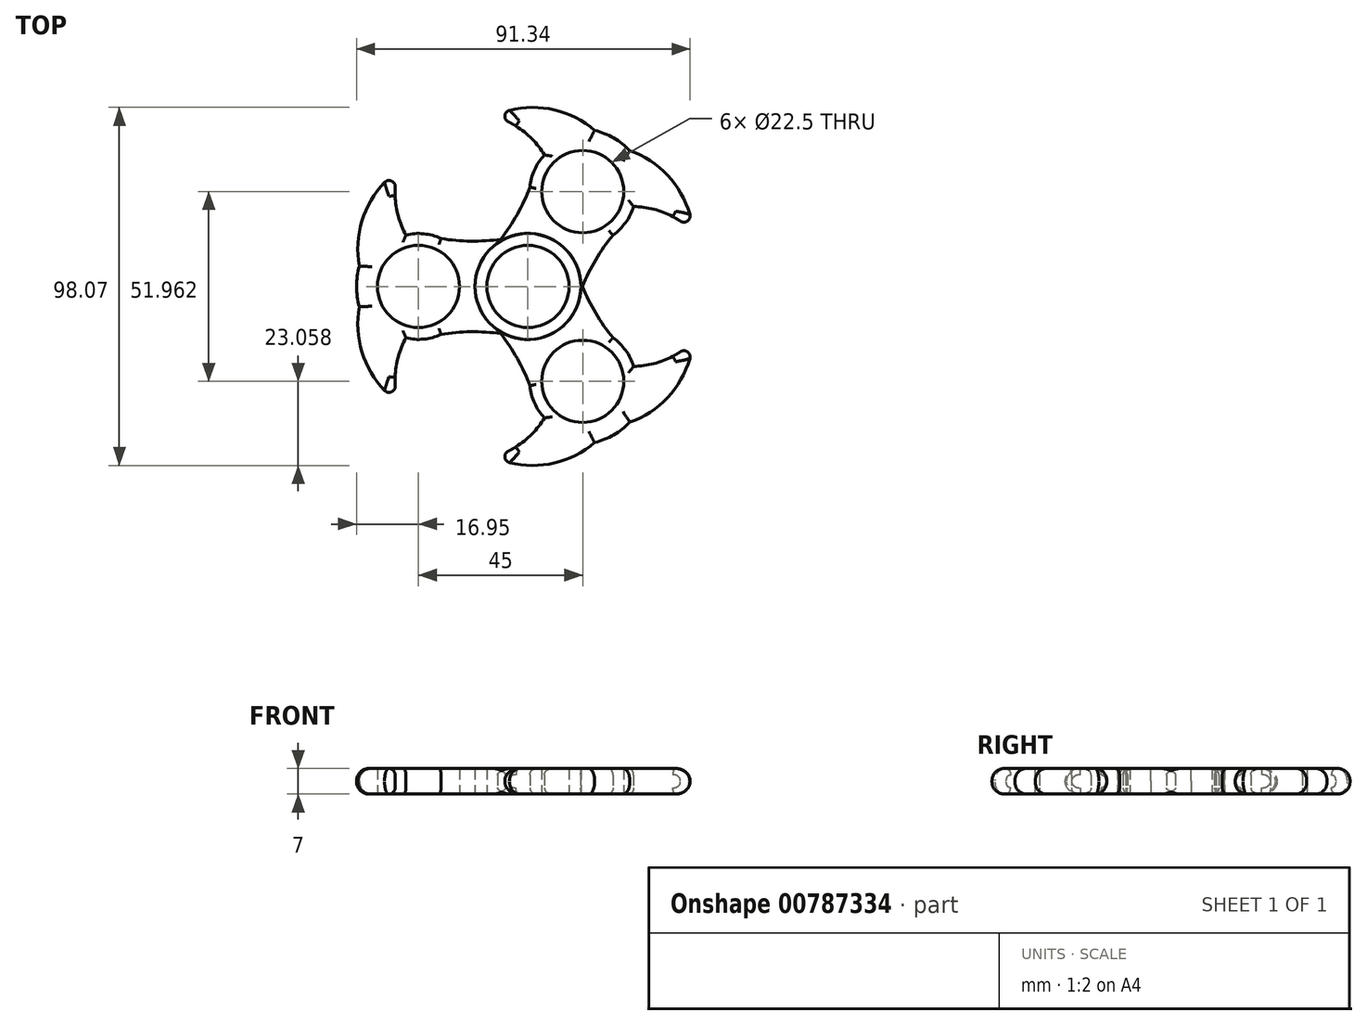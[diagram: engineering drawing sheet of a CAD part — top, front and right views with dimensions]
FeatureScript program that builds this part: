
annotation { "Feature Type Name" : "Feature", "Feature Type Description" : "" }
export const myFeature = defineFeature(function(context is Context, id is Id, definition is map)
    precondition{}
    {
        {
            var Q0;
            Q0=qCreatedBy(makeId("Top.planeOp"),FACE);
            var sketch = newSketch(context, id + "F0", { "sketchPlane" : qUnion([Q0])});
            skCircle(sketch, "E0", {"center": v(0, 0) * mm, "radius": 11.25 * mm});
            skLineSegment(sketch, "E1", {"start": v(0, 0) * mm, "end": v(-30, 0) * mm});
            skCircle(sketch, "E2", {"center": v(-30, 0) * mm, "radius": 11.25 * mm});
            skCircle(sketch, "E3", {"center": v(-30, 0) * mm, "radius": 14.5 * mm});
            skCircle(sketch, "E4", {"center": v(0, 0) * mm, "radius": 14.5 * mm});
            skArc(sketch, "E5", {"start": v(0, -14.5) * mm, "mid": v(-15, -12.4) * mm, "end": v(-30, -14.5) * mm});
            skArc(sketch, "E6.MirrorCS", {"start": v(0, 14.5) * mm, "mid": v(-15, 12.41) * mm, "end": v(-30, 14.5) * mm});
            skArc(sketch, "E7", {"start": v(-33.43, -14.08) * mm, "mid": v(-36.22, -22.63) * mm, "end": v(-35.67, -31.61) * mm});
            skArc(sketch, "E8", {"start": v(-44.5, 0) * mm, "mid": v(-45.64, -17.36) * mm, "end": v(-35.67, -31.61) * mm});
            skArc(sketch, "E9.MirrorCS", {"start": v(-33.43, 14.1) * mm, "mid": v(-36.22, 22.65) * mm, "end": v(-35.67, 31.63) * mm});
            skArc(sketch, "E10.MirrorCS", {"start": v(-44.5, 0.02) * mm, "mid": v(-45.64, 17.38) * mm, "end": v(-35.67, 31.63) * mm});
            skLineSegment(sketch, "E11", {"start": v(-44.5, 0.02) * mm, "end": v(-46.18, 0.02) * mm});
            skArc(sketch, "E12", {"start": v(-46.18, 5.59) * mm, "mid": v(-46.95, 0) * mm, "end": v(-46.18, -5.57) * mm});
            skSolve(sketch);
        }
        {
            var Q0;
            Q0=qSketchRegion(id+"F0",true);
            extrude(context, id + "F1", {"entities" : qUnion([Q0]), "depth" : 7 * mm, "offsetDistance" : 25 * mm});
        }
        {
            var Q0;
            Q0=makeQuery(id+"F1.opExtrude","SWEPT_BODY",BODY,{"disambiguationData":[OSD([sQuery(id+"F0.wireOp",EDGE,"E0"),sQuery(id+"F0.wireOp",EDGE,"E2"),sQuery(id+"F0.wireOp",EDGE,"E3"),sQuery(id+"F0.wireOp",EDGE,"E4"),sQuery(id+"F0.wireOp",EDGE,"E5"),sQuery(id+"F0.wireOp",EDGE,"E6.MirrorCS"),sQuery(id+"F0.wireOp",EDGE,"N5z0aknD-i1vi-YF0C-1aPX-2y42hYEXv3Ia"),sQuery(id+"F0.wireOp",EDGE,"vDmnVq8P-OYbs-Mt9C-JsBL-gKGyEo7dJEWc")])]});
            var Q1;
            Q1=makeQuery(id+"F1.opExtrude","SWEPT_FACE",FACE,{"disambiguationData":[OSD([sQuery(id+"F0.wireOp",EDGE,"E4")])]});
            circularPattern(context, id + "F2", {"entities" : qUnion([Q0]), "axis" : qUnion([Q1]), "angle" : 360 * degree, "instanceCount" : 3, "equalSpace" : true});
        }
        {
            var Q0;
            Q0=makeQuery(id+"F2.opPattern","COPY",EDGE,{"derivedFrom":makeQuery(id+"F1.opExtrude","CAP_EDGE",EDGE,{"disambiguationData":[OSD([sQuery(id+"F0.wireOp",EDGE,"E10.MirrorCS")])],"isStart":false}),"instanceName":"2"});
            var Q1;
            Q1=makeQuery(id+"F2.opPattern","COPY",EDGE,{"derivedFrom":makeQuery(id+"F1.opExtrude","CAP_EDGE",EDGE,{"disambiguationData":[OSD([sQuery(id+"F0.wireOp",EDGE,"E12")])],"isStart":false}),"instanceName":"2"});
            var Q2;
            Q2=makeQuery(id+"F2.opPattern","COPY",EDGE,{"derivedFrom":makeQuery(id+"F1.opExtrude","CAP_EDGE",EDGE,{"disambiguationData":[OSD([sQuery(id+"F0.wireOp",EDGE,"E8")])],"isStart":false}),"instanceName":"2"});
            var Q3;
            Q3=makeQuery(id+"F2.opPattern","COPY",EDGE,{"derivedFrom":makeQuery(id+"F1.opExtrude","CAP_EDGE",EDGE,{"disambiguationData":[OSD([sQuery(id+"F0.wireOp",EDGE,"E10.MirrorCS")])],"isStart":false}),"instanceName":"1"});
            var Q4;
            Q4=makeQuery(id+"F2.opPattern","COPY",EDGE,{"derivedFrom":makeQuery(id+"F1.opExtrude","CAP_EDGE",EDGE,{"disambiguationData":[OSD([sQuery(id+"F0.wireOp",EDGE,"E12")])],"isStart":false}),"instanceName":"1"});
            var Q5;
            Q5=makeQuery(id+"F2.opPattern","COPY",EDGE,{"derivedFrom":makeQuery(id+"F1.opExtrude","CAP_EDGE",EDGE,{"disambiguationData":[OSD([sQuery(id+"F0.wireOp",EDGE,"E8")])],"isStart":false}),"instanceName":"1"});
            var Q6;
            Q6=makeQuery(id+"F1.opExtrude","CAP_EDGE",EDGE,{"disambiguationData":[OSD([sQuery(id+"F0.wireOp",EDGE,"E10.MirrorCS")])],"isStart":false});
            var Q7;
            Q7=makeQuery(id+"F1.opExtrude","CAP_EDGE",EDGE,{"disambiguationData":[OSD([sQuery(id+"F0.wireOp",EDGE,"E12")])],"isStart":false});
            var Q8;
            Q8=makeQuery(id+"F1.opExtrude","CAP_EDGE",EDGE,{"disambiguationData":[OSD([sQuery(id+"F0.wireOp",EDGE,"E8")])],"isStart":false});
            var Q9;
            Q9=makeQuery(id+"F1.opExtrude","CAP_EDGE",EDGE,{"disambiguationData":[OSD([sQuery(id+"F0.wireOp",EDGE,"E12")])],"isStart":true});
            var Q10;
            Q10=makeQuery(id+"F1.opExtrude","CAP_EDGE",EDGE,{"disambiguationData":[OSD([sQuery(id+"F0.wireOp",EDGE,"E8")])],"isStart":true});
            var Q11;
            Q11=makeQuery(id+"F1.opExtrude","CAP_EDGE",EDGE,{"disambiguationData":[OSD([sQuery(id+"F0.wireOp",EDGE,"E10.MirrorCS")])],"isStart":true});
            var Q12;
            Q12=makeQuery(id+"F2.opPattern","COPY",EDGE,{"derivedFrom":makeQuery(id+"F1.opExtrude","CAP_EDGE",EDGE,{"disambiguationData":[OSD([sQuery(id+"F0.wireOp",EDGE,"E12")])],"isStart":true}),"instanceName":"2"});
            var Q13;
            Q13=makeQuery(id+"F2.opPattern","COPY",EDGE,{"derivedFrom":makeQuery(id+"F1.opExtrude","CAP_EDGE",EDGE,{"disambiguationData":[OSD([sQuery(id+"F0.wireOp",EDGE,"E8")])],"isStart":true}),"instanceName":"2"});
            var Q14;
            Q14=makeQuery(id+"F2.opPattern","COPY",EDGE,{"derivedFrom":makeQuery(id+"F1.opExtrude","CAP_EDGE",EDGE,{"disambiguationData":[OSD([sQuery(id+"F0.wireOp",EDGE,"E10.MirrorCS")])],"isStart":true}),"instanceName":"2"});
            var Q15;
            Q15=makeQuery(id+"F2.opPattern","COPY",EDGE,{"derivedFrom":makeQuery(id+"F1.opExtrude","CAP_EDGE",EDGE,{"disambiguationData":[OSD([sQuery(id+"F0.wireOp",EDGE,"E10.MirrorCS")])],"isStart":true}),"instanceName":"1"});
            var Q16;
            Q16=makeQuery(id+"F2.opPattern","COPY",EDGE,{"derivedFrom":makeQuery(id+"F1.opExtrude","CAP_EDGE",EDGE,{"disambiguationData":[OSD([sQuery(id+"F0.wireOp",EDGE,"E12")])],"isStart":true}),"instanceName":"1"});
            var Q17;
            Q17=makeQuery(id+"F2.opPattern","COPY",EDGE,{"derivedFrom":makeQuery(id+"F1.opExtrude","CAP_EDGE",EDGE,{"disambiguationData":[OSD([sQuery(id+"F0.wireOp",EDGE,"E8")])],"isStart":true}),"instanceName":"1"});
            fillet(context, id + "F3", {"entities" : qUnion([Q0, Q1, Q2, Q3, Q4, Q5, Q6, Q7, Q8, Q9, Q10, Q11, Q12, Q13, Q14, Q15, Q16, Q17]), "radius" : 3.38 * mm, "tangentPropagation" : true, "allowEdgeOverflow" : false});
        }
        {
            var Q0;
            Q0=makeQuery(id+"F2.opPattern","COPY",EDGE,{"derivedFrom":makeQuery(id+"F1.opExtrude","CAP_EDGE",EDGE,{"disambiguationData":[OSD([sQuery(id+"F0.wireOp",EDGE,"E6.MirrorCS")])],"isStart":true}),"instanceName":"2"});
            var Q1;
            Q1=makeQuery(id+"F1.opExtrude","CAP_EDGE",EDGE,{"disambiguationData":[OSD([sQuery(id+"F0.wireOp",EDGE,"E5")])],"isStart":true});
            var Q2;
            Q2=makeQuery(id+"F2.opPattern","COPY",EDGE,{"derivedFrom":makeQuery(id+"F1.opExtrude","CAP_EDGE",EDGE,{"disambiguationData":[OSD([sQuery(id+"F0.wireOp",EDGE,"E5")])],"isStart":true}),"instanceName":"2"});
            var Q3;
            Q3=makeQuery(id+"F2.opPattern","COPY",EDGE,{"derivedFrom":makeQuery(id+"F1.opExtrude","CAP_EDGE",EDGE,{"disambiguationData":[OSD([sQuery(id+"F0.wireOp",EDGE,"E6.MirrorCS")])],"isStart":true}),"instanceName":"1"});
            var Q4;
            Q4=makeQuery(id+"F2.opPattern","COPY",EDGE,{"derivedFrom":makeQuery(id+"F1.opExtrude","CAP_EDGE",EDGE,{"disambiguationData":[OSD([sQuery(id+"F0.wireOp",EDGE,"E5")])],"isStart":true}),"instanceName":"1"});
            var Q5;
            Q5=makeQuery(id+"F1.opExtrude","CAP_EDGE",EDGE,{"disambiguationData":[OSD([sQuery(id+"F0.wireOp",EDGE,"E6.MirrorCS")])],"isStart":true});
            var Q6;
            {var subQ0=sQuery(id+"F0.wireOp",EDGE,"E6.MirrorCS");var subQ1=sQuery(id+"F0.wireOp",EDGE,"E3");var subQ2=makeQuery(id+"F0.imprint","INTERSECT",VERTEX,{"disambiguationData":[OD(0.0)],"derivedFrom":[subQ1,subQ0]});Q6=makeQuery(id+"F1.opExtrude","CAP_EDGE",EDGE,{"disambiguationData":[OSD([subQ1]),TDD([makeQuery(id+"F0.imprint","IMPRINT",EDGE,{"disambiguationData":[TD([[subQ2,1.0]])],"derivedFrom":subQ1}),makeQuery(id+"F0.imprint","IMPRINT",EDGE,{"disambiguationData":[TD([[subQ2,-1.0]])],"derivedFrom":subQ1})])],"isStart":true});}
            var Q7;
            {var subQ0=sQuery(id+"F0.wireOp",EDGE,"E5");var subQ1=sQuery(id+"F0.wireOp",EDGE,"E3");var subQ2=makeQuery(id+"F0.imprint","INTERSECT",VERTEX,{"disambiguationData":[OD(0.0)],"derivedFrom":[subQ1,subQ0]});Q7=makeQuery(id+"F2.opPattern","COPY",EDGE,{"derivedFrom":makeQuery(id+"F1.opExtrude","CAP_EDGE",EDGE,{"disambiguationData":[OSD([subQ1]),TDD([makeQuery(id+"F0.imprint","IMPRINT",EDGE,{"disambiguationData":[TD([[subQ2,1.0]])],"derivedFrom":subQ1}),makeQuery(id+"F0.imprint","IMPRINT",EDGE,{"disambiguationData":[TD([[subQ2,-1.0]])],"derivedFrom":subQ1})])],"isStart":true}),"instanceName":"1"});}
            var Q8;
            {var subQ0=sQuery(id+"F0.wireOp",EDGE,"E6.MirrorCS");var subQ1=sQuery(id+"F0.wireOp",EDGE,"E3");var subQ2=makeQuery(id+"F0.imprint","INTERSECT",VERTEX,{"disambiguationData":[OD(0.0)],"derivedFrom":[subQ1,subQ0]});Q8=makeQuery(id+"F2.opPattern","COPY",EDGE,{"derivedFrom":makeQuery(id+"F1.opExtrude","CAP_EDGE",EDGE,{"disambiguationData":[OSD([subQ1]),TDD([makeQuery(id+"F0.imprint","IMPRINT",EDGE,{"disambiguationData":[TD([[subQ2,1.0]])],"derivedFrom":subQ1}),makeQuery(id+"F0.imprint","IMPRINT",EDGE,{"disambiguationData":[TD([[subQ2,-1.0]])],"derivedFrom":subQ1})])],"isStart":true}),"instanceName":"1"});}
            var Q9;
            {var subQ0=sQuery(id+"F0.wireOp",EDGE,"E6.MirrorCS");var subQ1=sQuery(id+"F0.wireOp",EDGE,"E3");var subQ2=makeQuery(id+"F0.imprint","INTERSECT",VERTEX,{"disambiguationData":[OD(0.0)],"derivedFrom":[subQ1,subQ0]});Q9=makeQuery(id+"F2.opPattern","COPY",EDGE,{"derivedFrom":makeQuery(id+"F1.opExtrude","CAP_EDGE",EDGE,{"disambiguationData":[OSD([subQ1]),TDD([makeQuery(id+"F0.imprint","IMPRINT",EDGE,{"disambiguationData":[TD([[subQ2,1.0]])],"derivedFrom":subQ1}),makeQuery(id+"F0.imprint","IMPRINT",EDGE,{"disambiguationData":[TD([[subQ2,-1.0]])],"derivedFrom":subQ1})])],"isStart":true}),"instanceName":"2"});}
            var Q10;
            {var subQ0=sQuery(id+"F0.wireOp",EDGE,"E5");var subQ1=sQuery(id+"F0.wireOp",EDGE,"E3");var subQ2=makeQuery(id+"F0.imprint","INTERSECT",VERTEX,{"disambiguationData":[OD(0.0)],"derivedFrom":[subQ1,subQ0]});Q10=makeQuery(id+"F1.opExtrude","CAP_EDGE",EDGE,{"disambiguationData":[OSD([subQ1]),TDD([makeQuery(id+"F0.imprint","IMPRINT",EDGE,{"disambiguationData":[TD([[subQ2,1.0]])],"derivedFrom":subQ1}),makeQuery(id+"F0.imprint","IMPRINT",EDGE,{"disambiguationData":[TD([[subQ2,-1.0]])],"derivedFrom":subQ1})])],"isStart":true});}
            var Q11;
            {var subQ0=sQuery(id+"F0.wireOp",EDGE,"E5");var subQ1=sQuery(id+"F0.wireOp",EDGE,"E3");var subQ2=makeQuery(id+"F0.imprint","INTERSECT",VERTEX,{"disambiguationData":[OD(0.0)],"derivedFrom":[subQ1,subQ0]});Q11=makeQuery(id+"F2.opPattern","COPY",EDGE,{"derivedFrom":makeQuery(id+"F1.opExtrude","CAP_EDGE",EDGE,{"disambiguationData":[OSD([subQ1]),TDD([makeQuery(id+"F0.imprint","IMPRINT",EDGE,{"disambiguationData":[TD([[subQ2,1.0]])],"derivedFrom":subQ1}),makeQuery(id+"F0.imprint","IMPRINT",EDGE,{"disambiguationData":[TD([[subQ2,-1.0]])],"derivedFrom":subQ1})])],"isStart":true}),"instanceName":"2"});}
            var Q12;
            {var subQ0=sQuery(id+"F0.wireOp",EDGE,"E6.MirrorCS");var subQ1=sQuery(id+"F0.wireOp",EDGE,"E3");var subQ2=makeQuery(id+"F0.imprint","INTERSECT",VERTEX,{"disambiguationData":[OD(0.0)],"derivedFrom":[subQ1,subQ0]});Q12=makeQuery(id+"F2.opPattern","COPY",EDGE,{"derivedFrom":makeQuery(id+"F1.opExtrude","CAP_EDGE",EDGE,{"disambiguationData":[OSD([subQ1]),TDD([makeQuery(id+"F0.imprint","IMPRINT",EDGE,{"disambiguationData":[TD([[subQ2,1.0]])],"derivedFrom":subQ1}),makeQuery(id+"F0.imprint","IMPRINT",EDGE,{"disambiguationData":[TD([[subQ2,-1.0]])],"derivedFrom":subQ1})])],"isStart":false}),"instanceName":"2"});}
            var Q13;
            Q13=makeQuery(id+"F2.opPattern","COPY",EDGE,{"derivedFrom":makeQuery(id+"F1.opExtrude","CAP_EDGE",EDGE,{"disambiguationData":[OSD([sQuery(id+"F0.wireOp",EDGE,"E6.MirrorCS")])],"isStart":false}),"instanceName":"2"});
            var Q14;
            Q14=makeQuery(id+"F1.opExtrude","CAP_EDGE",EDGE,{"disambiguationData":[OSD([sQuery(id+"F0.wireOp",EDGE,"E5")])],"isStart":false});
            var Q15;
            {var subQ0=sQuery(id+"F0.wireOp",EDGE,"E5");var subQ1=sQuery(id+"F0.wireOp",EDGE,"E3");var subQ2=makeQuery(id+"F0.imprint","INTERSECT",VERTEX,{"disambiguationData":[OD(0.0)],"derivedFrom":[subQ1,subQ0]});Q15=makeQuery(id+"F1.opExtrude","CAP_EDGE",EDGE,{"disambiguationData":[OSD([subQ1]),TDD([makeQuery(id+"F0.imprint","IMPRINT",EDGE,{"disambiguationData":[TD([[subQ2,1.0]])],"derivedFrom":subQ1}),makeQuery(id+"F0.imprint","IMPRINT",EDGE,{"disambiguationData":[TD([[subQ2,-1.0]])],"derivedFrom":subQ1})])],"isStart":false});}
            var Q16;
            Q16=makeQuery(id+"F1.opExtrude","CAP_EDGE",EDGE,{"disambiguationData":[OSD([sQuery(id+"F0.wireOp",EDGE,"E6.MirrorCS")])],"isStart":false});
            var Q17;
            {var subQ0=sQuery(id+"F0.wireOp",EDGE,"E6.MirrorCS");var subQ1=sQuery(id+"F0.wireOp",EDGE,"E3");var subQ2=makeQuery(id+"F0.imprint","INTERSECT",VERTEX,{"disambiguationData":[OD(0.0)],"derivedFrom":[subQ1,subQ0]});Q17=makeQuery(id+"F1.opExtrude","CAP_EDGE",EDGE,{"disambiguationData":[OSD([subQ1]),TDD([makeQuery(id+"F0.imprint","IMPRINT",EDGE,{"disambiguationData":[TD([[subQ2,1.0]])],"derivedFrom":subQ1}),makeQuery(id+"F0.imprint","IMPRINT",EDGE,{"disambiguationData":[TD([[subQ2,-1.0]])],"derivedFrom":subQ1})])],"isStart":false});}
            var Q18;
            Q18=makeQuery(id+"F2.opPattern","COPY",EDGE,{"derivedFrom":makeQuery(id+"F1.opExtrude","CAP_EDGE",EDGE,{"disambiguationData":[OSD([sQuery(id+"F0.wireOp",EDGE,"E5")])],"isStart":false}),"instanceName":"1"});
            var Q19;
            {var subQ0=sQuery(id+"F0.wireOp",EDGE,"E5");var subQ1=sQuery(id+"F0.wireOp",EDGE,"E3");var subQ2=makeQuery(id+"F0.imprint","INTERSECT",VERTEX,{"disambiguationData":[OD(0.0)],"derivedFrom":[subQ1,subQ0]});Q19=makeQuery(id+"F2.opPattern","COPY",EDGE,{"derivedFrom":makeQuery(id+"F1.opExtrude","CAP_EDGE",EDGE,{"disambiguationData":[OSD([subQ1]),TDD([makeQuery(id+"F0.imprint","IMPRINT",EDGE,{"disambiguationData":[TD([[subQ2,1.0]])],"derivedFrom":subQ1}),makeQuery(id+"F0.imprint","IMPRINT",EDGE,{"disambiguationData":[TD([[subQ2,-1.0]])],"derivedFrom":subQ1})])],"isStart":false}),"instanceName":"1"});}
            var Q20;
            Q20=makeQuery(id+"F2.opPattern","COPY",EDGE,{"derivedFrom":makeQuery(id+"F1.opExtrude","CAP_EDGE",EDGE,{"disambiguationData":[OSD([sQuery(id+"F0.wireOp",EDGE,"E6.MirrorCS")])],"isStart":false}),"instanceName":"1"});
            var Q21;
            Q21=makeQuery(id+"F2.opPattern","COPY",EDGE,{"derivedFrom":makeQuery(id+"F1.opExtrude","CAP_EDGE",EDGE,{"disambiguationData":[OSD([sQuery(id+"F0.wireOp",EDGE,"E5")])],"isStart":false}),"instanceName":"2"});
            var Q22;
            {var subQ0=sQuery(id+"F0.wireOp",EDGE,"E5");var subQ1=sQuery(id+"F0.wireOp",EDGE,"E3");var subQ2=makeQuery(id+"F0.imprint","INTERSECT",VERTEX,{"disambiguationData":[OD(0.0)],"derivedFrom":[subQ1,subQ0]});Q22=makeQuery(id+"F2.opPattern","COPY",EDGE,{"derivedFrom":makeQuery(id+"F1.opExtrude","CAP_EDGE",EDGE,{"disambiguationData":[OSD([subQ1]),TDD([makeQuery(id+"F0.imprint","IMPRINT",EDGE,{"disambiguationData":[TD([[subQ2,1.0]])],"derivedFrom":subQ1}),makeQuery(id+"F0.imprint","IMPRINT",EDGE,{"disambiguationData":[TD([[subQ2,-1.0]])],"derivedFrom":subQ1})])],"isStart":false}),"instanceName":"2"});}
            var Q23;
            {var subQ0=sQuery(id+"F0.wireOp",EDGE,"E6.MirrorCS");var subQ1=sQuery(id+"F0.wireOp",EDGE,"E3");var subQ2=makeQuery(id+"F0.imprint","INTERSECT",VERTEX,{"disambiguationData":[OD(0.0)],"derivedFrom":[subQ1,subQ0]});Q23=makeQuery(id+"F2.opPattern","COPY",EDGE,{"derivedFrom":makeQuery(id+"F1.opExtrude","CAP_EDGE",EDGE,{"disambiguationData":[OSD([subQ1]),TDD([makeQuery(id+"F0.imprint","IMPRINT",EDGE,{"disambiguationData":[TD([[subQ2,1.0]])],"derivedFrom":subQ1}),makeQuery(id+"F0.imprint","IMPRINT",EDGE,{"disambiguationData":[TD([[subQ2,-1.0]])],"derivedFrom":subQ1})])],"isStart":false}),"instanceName":"1"});}
            var Q24;
            Q24=makeQuery(id+"F2.opPattern","COPY",EDGE,{"derivedFrom":makeQuery(id+"F1.opExtrude","CAP_EDGE",EDGE,{"disambiguationData":[OSD([sQuery(id+"F0.wireOp",EDGE,"E9.MirrorCS")])],"isStart":false}),"instanceName":"2"});
            var Q25;
            Q25=makeQuery(id+"F2.opPattern","COPY",EDGE,{"derivedFrom":makeQuery(id+"F1.opExtrude","CAP_EDGE",EDGE,{"disambiguationData":[OSD([sQuery(id+"F0.wireOp",EDGE,"E9.MirrorCS")])],"isStart":true}),"instanceName":"2"});
            var Q26;
            Q26=makeQuery(id+"F1.opExtrude","CAP_EDGE",EDGE,{"disambiguationData":[OSD([sQuery(id+"F0.wireOp",EDGE,"E7")])],"isStart":false});
            var Q27;
            Q27=makeQuery(id+"F1.opExtrude","CAP_EDGE",EDGE,{"disambiguationData":[OSD([sQuery(id+"F0.wireOp",EDGE,"E7")])],"isStart":true});
            var Q28;
            Q28=makeQuery(id+"F1.opExtrude","CAP_EDGE",EDGE,{"disambiguationData":[OSD([sQuery(id+"F0.wireOp",EDGE,"E9.MirrorCS")])],"isStart":false});
            var Q29;
            Q29=makeQuery(id+"F2.opPattern","COPY",EDGE,{"derivedFrom":makeQuery(id+"F1.opExtrude","CAP_EDGE",EDGE,{"disambiguationData":[OSD([sQuery(id+"F0.wireOp",EDGE,"E9.MirrorCS")])],"isStart":false}),"instanceName":"1"});
            var Q30;
            Q30=makeQuery(id+"F2.opPattern","COPY",EDGE,{"derivedFrom":makeQuery(id+"F1.opExtrude","CAP_EDGE",EDGE,{"disambiguationData":[OSD([sQuery(id+"F0.wireOp",EDGE,"E7")])],"isStart":false}),"instanceName":"2"});
            var Q31;
            Q31=makeQuery(id+"F2.opPattern","COPY",EDGE,{"derivedFrom":makeQuery(id+"F1.opExtrude","CAP_EDGE",EDGE,{"disambiguationData":[OSD([sQuery(id+"F0.wireOp",EDGE,"E7")])],"isStart":true}),"instanceName":"1"});
            fillet(context, id + "F4", {"entities" : qUnion([Q0, Q1, Q2, Q3, Q4, Q5, Q6, Q7, Q8, Q9, Q10, Q11, Q12, Q13, Q14, Q15, Q16, Q17, Q18, Q19, Q20, Q21, Q22, Q23, Q24, Q25, Q26, Q27, Q28, Q29, Q30, Q31]), "radius" : 1.69 * mm, "tangentPropagation" : true, "allowEdgeOverflow" : false});
        }
    });
